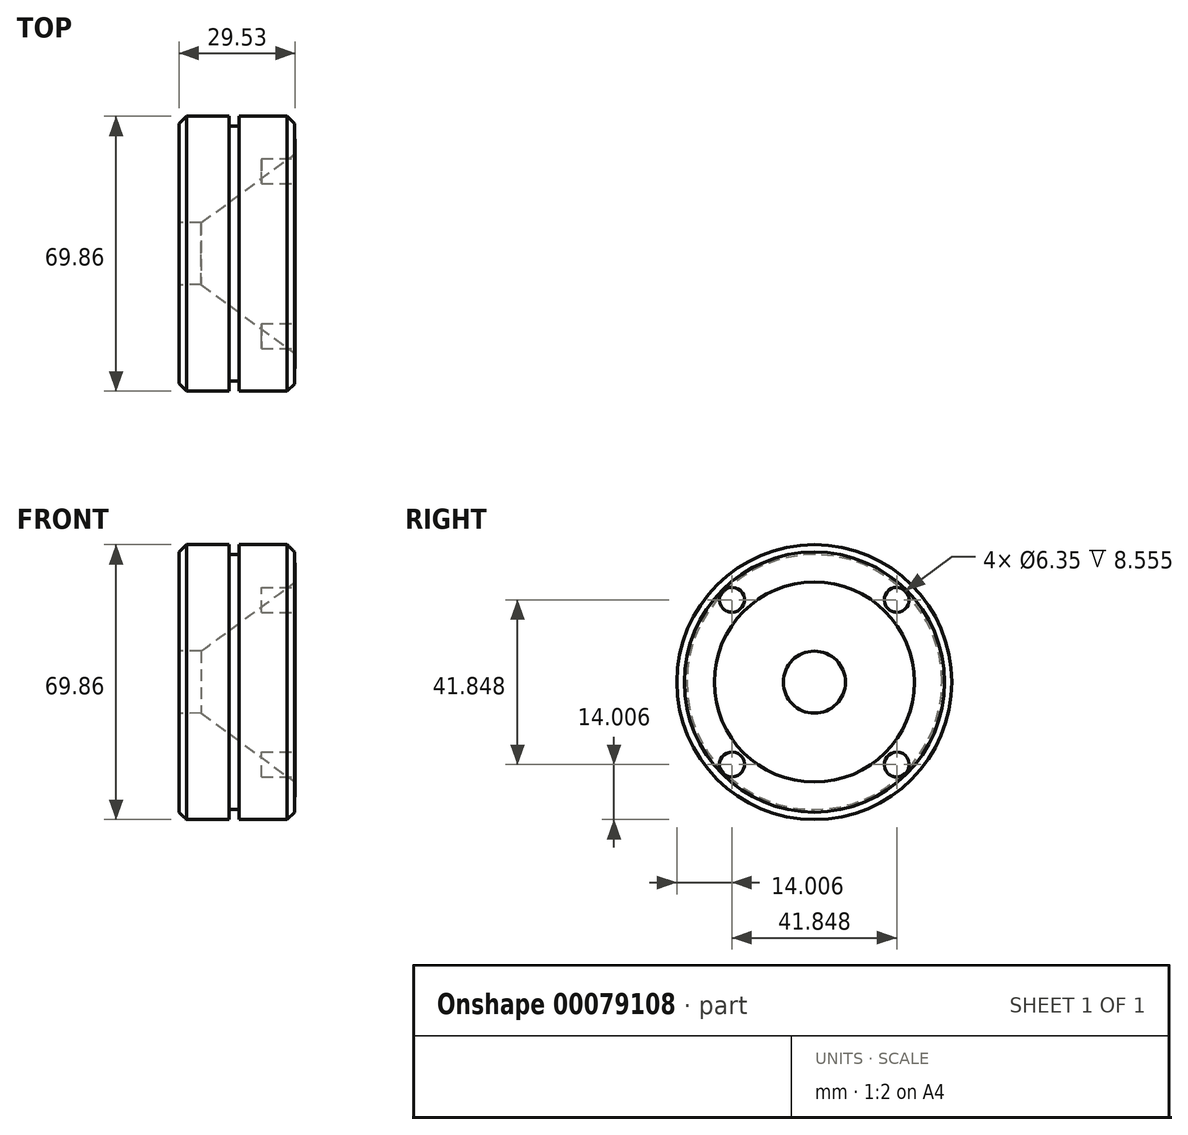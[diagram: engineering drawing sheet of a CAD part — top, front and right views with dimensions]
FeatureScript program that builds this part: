
annotation { "Feature Type Name" : "Feature", "Feature Type Description" : "" }
export const myFeature = defineFeature(function(context is Context, id is Id, definition is map)
    precondition{}
    {
        {
            var Q0;
            Q0=qCreatedBy(makeId("Front.planeOp"),FACE);
            var sketch = newSketch(context, id + "F0", { "sketchPlane" : qUnion([Q0])});
            skLineSegment(sketch, "E0", {"start": v(5.66, 7.89) * mm, "end": v(29.53, 25.4) * mm});
            skLineSegment(sketch, "E1", {"start": v(29.34, 34.93) * mm, "end": v(15.32, 34.93) * mm});
            skLineSegment(sketch, "E2", {"start": v(15.32, 34.93) * mm, "end": v(15.32, 32.39) * mm});
            skLineSegment(sketch, "E3", {"start": v(15.32, 32.39) * mm, "end": v(12.7, 32.39) * mm});
            skLineSegment(sketch, "E4", {"start": v(12.7, 32.39) * mm, "end": v(12.7, 34.93) * mm});
            skLineSegment(sketch, "E5", {"start": v(12.7, 34.93) * mm, "end": v(0, 34.93) * mm});
            skLineSegment(sketch, "E6", {"start": v(0, 34.93) * mm, "end": v(0, 7.94) * mm});
            skLineSegment(sketch, "E7", {"start": v(29.53, 25.4) * mm, "end": v(29.34, 34.93) * mm});
            skLineSegment(sketch, "E8", {"start": v(5.66, 7.89) * mm, "end": v(0, 7.94) * mm});
            skLineSegment(sketch, "E9", {"start": v(0, 0) * mm, "end": v(20.44, 0) * mm});
            skSolve(sketch);
        }
        {
            var Q0;
            Q0=makeQuery(id+"F0.imprint","IMPRINT",FACE,{"disambiguationData":[TD([[makeQuery(id+"F0.imprint","IMPRINT",EDGE,{"derivedFrom":sQuery(id+"F0.wireOp",EDGE,"E0")}),1.0]])]});
            var Q1;
            Q1=sQuery(id+"F0.wireOp",EDGE,"E9");
            revolve(context, id + "F1", {"entities" : qUnion([Q0]), "axis" : qUnion([Q1]), "revolveType" : RevolveType.FULL});
        }
        {
            var Q0;
            Q0=makeQuery(id+"F1.opRevolve","SWEPT_EDGE",EDGE,{"disambiguationData":[OSD([sQuery(id+"F0.wireOp",EDGE,"E5"),sQuery(id+"F0.wireOp",EDGE,"E6")])]});
            var Q1;
            Q1=makeQuery(id+"F1.opRevolve","SWEPT_EDGE",EDGE,{"disambiguationData":[OSD([sQuery(id+"F0.wireOp",EDGE,"E1"),sQuery(id+"F0.wireOp",EDGE,"E7")])]});
            chamfer(context, id + "F2", {"entities" : qUnion([Q0, Q1]), "width" : 1.9 * mm, "tangentPropagation" : true});
        }
        {
            var Q0;
            Q0=qCreatedBy(makeId("Right.planeOp"),FACE);
            cPlane(context, id + "F3", {"entities" : qUnion([Q0]), "cplaneType" : CPlaneType.OFFSET, "offset" : 33.65 * mm, "width" : 152.4 * mm, "height" : 152.4 * mm});
        }
        {
            var Q0;
            Q0=qCreatedBy(id+"F3.planeOp",FACE);
            var sketch = newSketch(context, id + "F4", { "sketchPlane" : qUnion([Q0])});
            skPoint(sketch, "E10.middle", {"position": v(0, 0) * mm});
            skCircle(sketch, "E11", {"center": v(20.92, 20.92) * mm, "radius": 3.18 * mm});
            skCircle(sketch, "E12", {"center": v(20.92, -20.92) * mm, "radius": 3.18 * mm});
            skCircle(sketch, "E13", {"center": v(-20.92, -20.92) * mm, "radius": 3.18 * mm});
            skCircle(sketch, "E14", {"center": v(-20.92, 20.92) * mm, "radius": 3.18 * mm});
            skSolve(sketch);
        }
        {
            var Q0;
            Q0 = qSketchRegion(id + "F4", true);
            extrude(context, id + "F5", {"entities" : qUnion([Q0]), "operationType" : NewBodyOperationType.REMOVE, "oppositeDirection" : true, "depth" : 12.7 * mm});
        }
    });
